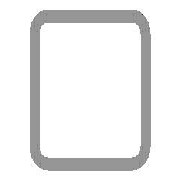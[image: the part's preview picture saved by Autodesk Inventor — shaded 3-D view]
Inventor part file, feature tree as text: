
AUTODESK INVENTOR PART (.ipt)
format: ipt  version: 2022 (Build 260153000, 153)  size: 553,984 bytes
history: native  units: mm (DEFAULTED — no unit token found)
features: other x11, surface_op x4, sketch x2, sweep x1, plane x1
ambient origin geometry x8: Origin, YZ Plane, XZ Plane, XY Plane, X Axis, Y Axis, Z Axis, Center Point
bodies: Body (feature_tree), Solid27 (feature_tree), Solid28 (feature_tree)
feature tree (19):
  parser-record x1  (decoder bookkeeping rows leaked as tree rows — omitted from the tree; the rows remain in map.json)
  other  "Driven Length"
  other  "Start Plane"
  other  "End Plane"
  sweep  "Sweep Path"
  other  "Orientation Work Plane"
  sketch  "Sketch3"  dims[d7=7.5mm d10=40.0mm]
  plane  "Work Plane3"
  sketch  "Sketch4"  dims[d11=40.0mm d12=5.0mm d13=-0.0mm d14=2899.411255mm d15=20.0mm d16=20.0mm d17=90.0deg d18=2899.411255mm d19=0.0mm d20=0.0mm d471=5.0mm d472=5.0mm d473=5.0mm d474=5.0mm d475=5.0mm d476=5.0mm d477=5.0mm d478=5.0mm d479=0.0mm d480=5.0mm d481=5.0mm d482=5.0mm d483=5.0mm d484=5.0mm d485=5.0mm d486=5.0mm d487=5.0mm d488=0.0mm d489=5.0mm d490=5.0mm d491=5.0mm d492=5.0mm d493=5.0mm d494=5.0mm d495=5.0mm d496=5.0mm d497=0.0mm d498=5.0mm d499=5.0mm d500=5.0mm d501=5.0mm d502=5.0mm d503=5.0mm d504=5.0mm d505=5.0mm d506=0.0mm]
  other  "Srf77"
  other  "Srf78"
  other  "Srf80"
  other  "Srf81"
  other  "Srf76"
  surface_op  "Boundary Patch51"
  surface_op  "Boundary Patch52"
  other  "Srf79"
  surface_op  "Boundary Patch53"
  surface_op  "Boundary Patch54"
